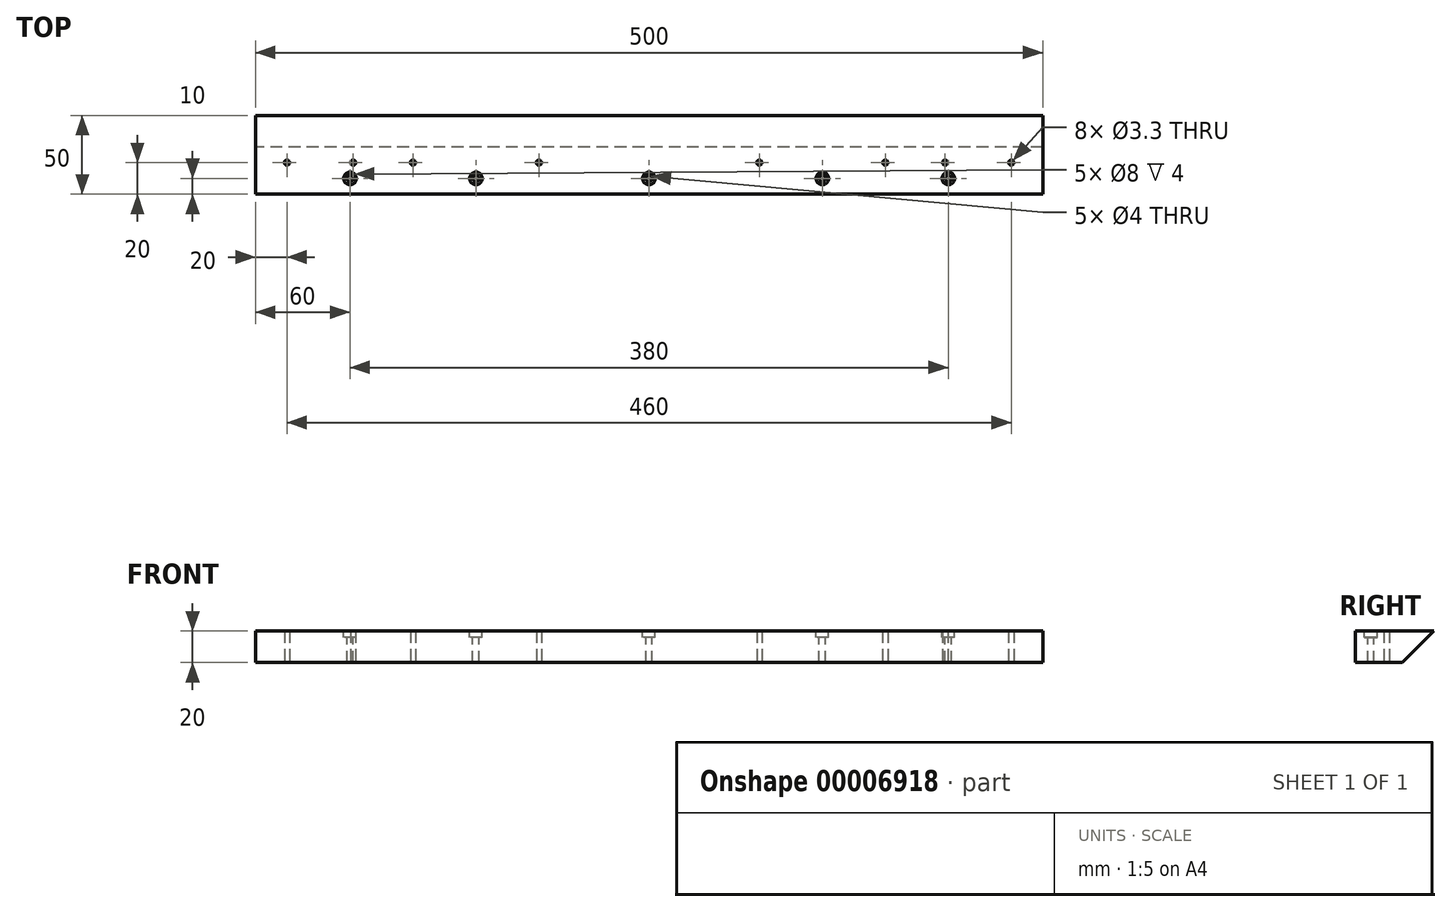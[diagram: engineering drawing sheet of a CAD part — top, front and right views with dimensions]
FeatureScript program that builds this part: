
annotation { "Feature Type Name" : "Feature", "Feature Type Description" : "" }
export const myFeature = defineFeature(function(context is Context, id is Id, definition is map)
    precondition{}
    {
        {
            var Q0;
            Q0=qCreatedBy(makeId("Top.planeOp"),FACE);
            var sketch = newSketch(context, id + "F0", { "sketchPlane" : qUnion([Q0])});
            skLineSegment(sketch, "E0.bottom", {"start": v(0, 0) * mm, "end": v(500, 0) * mm});
            skLineSegment(sketch, "E0.top", {"start": v(0, 50) * mm, "end": v(500, 50) * mm});
            skLineSegment(sketch, "E0.left", {"start": v(0, 0) * mm, "end": v(0, 50) * mm});
            skLineSegment(sketch, "E0.right", {"start": v(500, 0) * mm, "end": v(500, 50) * mm});
            skCircle(sketch, "E1", {"center": v(20, 20) * mm, "radius": 1.65 * mm});
            skCircle(sketch, "E2", {"center": v(100, 20) * mm, "radius": 1.65 * mm});
            skCircle(sketch, "E3", {"center": v(480, 20) * mm, "radius": 1.65 * mm});
            skCircle(sketch, "E4", {"center": v(400, 20) * mm, "radius": 1.65 * mm});
            skCircle(sketch, "E5", {"center": v(180, 20) * mm, "radius": 1.65 * mm});
            skCircle(sketch, "E6", {"center": v(320, 20) * mm, "radius": 1.65 * mm});
            skCircle(sketch, "E7", {"center": v(62, 20) * mm, "radius": 1.65 * mm});
            skCircle(sketch, "E8", {"center": v(438, 20) * mm, "radius": 1.65 * mm});
            skSolve(sketch);
        }
        {
            var Q0;
            Q0 = qSketchRegion(id + "F0", true);
            extrude(context, id + "F1", {"entities" : qUnion([Q0]), "depth" : (20) * mm});
        }
        {
            var Q0;
            Q0=makeQuery(id+"F1.opExtrude","SWEPT_FACE",FACE,{"disambiguationData":[OSD([sQuery(id+"F0.wireOp",EDGE,"E0.left")])]});
            var sketch = newSketch(context, id + "F2", { "sketchPlane" : qUnion([Q0])});
            skLineSegment(sketch, "E9", {"start": v(-50, 20) * mm, "end": v(-30, 0) * mm});
            skSolve(sketch);
        }
        {
            var Q0;
            {var subQ2=sQuery(id+"F2.wireOp",EDGE,"E9");Q0=makeQuery(id+"F2.imprint","IMPRINT",FACE,{"disambiguationData":[TD([[makeQuery(id+"F2.imprint","IMPRINT",EDGE,{"derivedFrom":subQ2}),-1.0]])]});}
            extrude(context, id + "F3", {"entities" : qUnion([Q0]), "operationType" : NewBodyOperationType.REMOVE, "endBound" : BoundingType.THROUGH_ALL, "oppositeDirection" : true, "depth" : 25 * mm});
        }
        {
            var Q0;
            Q0=makeQuery(id+"F1.opExtrude","CAP_FACE",FACE,{"disambiguationData":[OSD([sQuery(id+"F0.wireOp",EDGE,"E0.bottom"),sQuery(id+"F0.wireOp",EDGE,"E0.top"),sQuery(id+"F0.wireOp",EDGE,"E0.left"),sQuery(id+"F0.wireOp",EDGE,"E0.right"),sQuery(id+"F0.wireOp",EDGE,"E1"),sQuery(id+"F0.wireOp",EDGE,"E2"),sQuery(id+"F0.wireOp",EDGE,"E3"),sQuery(id+"F0.wireOp",EDGE,"E4"),sQuery(id+"F0.wireOp",EDGE,"E5"),sQuery(id+"F0.wireOp",EDGE,"E6")])],"isStart":false});
            var sketch = newSketch(context, id + "F4", { "sketchPlane" : qUnion([Q0])});
            skCircle(sketch, "E10", {"center": v(60, 10) * mm, "radius": 4 * mm});
            skCircle(sketch, "E11", {"center": v(140, 10) * mm, "radius": 4 * mm});
            skCircle(sketch, "E12", {"center": v(360, 10) * mm, "radius": 4 * mm});
            skCircle(sketch, "E13", {"center": v(440, 10) * mm, "radius": 4 * mm});
            skCircle(sketch, "E14", {"center": v(249.88, 10) * mm, "radius": 4 * mm});
            skLineSegment(sketch, "E15", {"start": v(250, 0) * mm, "end": v(249.88, 50) * mm, "construction": true});
            skSolve(sketch);
        }
        {
            var Q0;
            Q0 = qSketchRegion(id + "F4", true);
            extrude(context, id + "F5", {"entities" : qUnion([Q0]), "operationType" : NewBodyOperationType.REMOVE, "oppositeDirection" : true, "depth" : (4) * mm});
        }
        {
            var Q0;
            Q0=makeQuery(id+"F5.boolean.opBoolean","COPY",FACE,{"derivedFrom":makeQuery(id+"F5.opExtrude","CAP_FACE",FACE,{"disambiguationData":[OSD([sQuery(id+"F4.wireOp",EDGE,"E13")])],"isStart":false})});
            var sketch = newSketch(context, id + "F6", { "sketchPlane" : qUnion([Q0])});
            skCircle(sketch, "E16", {"center": v(440, 10) * mm, "radius": 2 * mm});
            skSolve(sketch);
        }
        {
            var Q0;
            Q0 = qSketchRegion(id + "F6", true);
            extrude(context, id + "F7", {"entities" : qUnion([Q0]), "operationType" : NewBodyOperationType.REMOVE, "endBound" : BoundingType.THROUGH_ALL, "oppositeDirection" : true, "depth" : 25 * mm});
        }
        {
            var Q0;
            Q0=makeQuery(id+"F5.boolean.opBoolean","COPY",FACE,{"derivedFrom":makeQuery(id+"F5.opExtrude","CAP_FACE",FACE,{"disambiguationData":[OSD([sQuery(id+"F4.wireOp",EDGE,"E12")])],"isStart":false})});
            var sketch = newSketch(context, id + "F8", { "sketchPlane" : qUnion([Q0])});
            skCircle(sketch, "E17", {"center": v(360, 10) * mm, "radius": 2 * mm});
            skSolve(sketch);
        }
        {
            var Q0;
            Q0 = qSketchRegion(id + "F8", true);
            extrude(context, id + "F9", {"entities" : qUnion([Q0]), "operationType" : NewBodyOperationType.REMOVE, "endBound" : BoundingType.THROUGH_ALL, "oppositeDirection" : true, "depth" : 25 * mm});
        }
        {
            var Q0;
            Q0=makeQuery(id+"F5.boolean.opBoolean","COPY",FACE,{"derivedFrom":makeQuery(id+"F5.opExtrude","CAP_FACE",FACE,{"disambiguationData":[OSD([sQuery(id+"F4.wireOp",EDGE,"E14")])],"isStart":false})});
            var sketch = newSketch(context, id + "F10", { "sketchPlane" : qUnion([Q0])});
            skCircle(sketch, "E18", {"center": v(249.88, 10) * mm, "radius": 2 * mm});
            skSolve(sketch);
        }
        {
            var Q0;
            Q0 = qSketchRegion(id + "F10", true);
            extrude(context, id + "F11", {"entities" : qUnion([Q0]), "operationType" : NewBodyOperationType.REMOVE, "endBound" : BoundingType.THROUGH_ALL, "oppositeDirection" : true, "depth" : 25 * mm});
        }
        {
            var Q0;
            Q0=makeQuery(id+"F5.boolean.opBoolean","COPY",FACE,{"derivedFrom":makeQuery(id+"F5.opExtrude","CAP_FACE",FACE,{"disambiguationData":[OSD([sQuery(id+"F4.wireOp",EDGE,"E11")])],"isStart":false})});
            var sketch = newSketch(context, id + "F12", { "sketchPlane" : qUnion([Q0])});
            skCircle(sketch, "E19", {"center": v(140, 10) * mm, "radius": 2 * mm});
            skSolve(sketch);
        }
        {
            var Q0;
            Q0 = qSketchRegion(id + "F12", true);
            extrude(context, id + "F13", {"entities" : qUnion([Q0]), "operationType" : NewBodyOperationType.REMOVE, "endBound" : BoundingType.THROUGH_ALL, "oppositeDirection" : true, "depth" : 25 * mm});
        }
        {
            var Q0;
            Q0=makeQuery(id+"F5.boolean.opBoolean","COPY",FACE,{"derivedFrom":makeQuery(id+"F5.opExtrude","CAP_FACE",FACE,{"disambiguationData":[OSD([sQuery(id+"F4.wireOp",EDGE,"E10")])],"isStart":false})});
            var sketch = newSketch(context, id + "F14", { "sketchPlane" : qUnion([Q0])});
            skCircle(sketch, "E20", {"center": v(60, 10) * mm, "radius": 2 * mm});
            skSolve(sketch);
        }
        {
            var Q0;
            Q0 = qSketchRegion(id + "F14", true);
            extrude(context, id + "F15", {"entities" : qUnion([Q0]), "operationType" : NewBodyOperationType.REMOVE, "endBound" : BoundingType.THROUGH_ALL, "oppositeDirection" : true, "depth" : 25 * mm});
        }
    });
